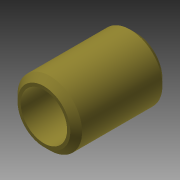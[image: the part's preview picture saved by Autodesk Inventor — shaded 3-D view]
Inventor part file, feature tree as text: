
AUTODESK INVENTOR PART (.ipt)
format: ipt  version: 2014 SP2 (Build 180246200, 246)  size: 113,664 bytes
history: native  units: in
note: dims shown in document units (in); Inventor stores cm internally (conversion verified against a paired STEP export)
features: other x35, revolve x1, sketch x1
ambient origin geometry x8: Origin, YZ Plane, XZ Plane, XY Plane, X Axis, Y Axis, Z Axis, Center Point
bodies: Solid1 (feature_tree)
feature tree (37):
  revolve  "Revolution1"  [1 undecoded]
  other  "bushing_XY"
  other  "bushing_YZ"
  other  "bushing_ZX"
  other  "bushing_X"
  other  "bushing_Y"
  other  "bushing_Z"
  other  "bushing_Center"
  other  "id1_XY"
  other  "id1_YZ"
  other  "id1_ZX"
  other  "id1_X"
  other  "id1_Y"
  other  "id1_Z"
  other  "id1_Center"
  other  "id2_XY"
  other  "id2_YZ"
  other  "id2_ZX"
  other  "id2_X"
  other  "id2_Y"
  other  "id2_Z"
  other  "id2_Center"
  other  "id3_XY"
  other  "id3_YZ"
  other  "id3_ZX"
  other  "id3_X"
  other  "id3_Y"
  other  "id3_Z"
  other  "id3_Center"
  other  "id4_XY"
  other  "id4_YZ"
  other  "id4_ZX"
  other  "id4_X"
  other  "id4_Y"
  other  "id4_Z"
  other  "id4_Center"
  sketch  "Sketch_1"  dims[d0=360.0deg d1=0.0in d2=0.0in]
note: 1 required parameter value undecoded (feature->parameter linkage not recoverable at this tier; creation-order binding heuristic only, values carry confidence <= 0.55)
